# Revit family: Legrand Marina versión vertical referencias 036910 a 036950
name_source: partatom
category: Installations électriques
revit_build: Autodesk Revit 2018 (Build: 20170223_1515(x64)
units: mm (PartAtom-declared; Revit-internal decimal feet)

## family parameters
Basée sur le plan de construction = Non
Conserver l'orientation des annotations = Non
Cote de connecteur circulaire = Utiliser le diamètre
Couper avec des vides une fois chargée = Non
Numéro OmniClass = 23.80.00.00
Partagée = Non
Point de calcul de pièce = Non
Titre OmniClass = Electric Power and Lighting
Toujours verticalement = Oui
Type d'élément = Normal

## types (23) — shared parameters
Condiciones Generales de Uso = https://export.legrand.com
ETIM Class 6.0 = EC000058
Fabricant = Legrand
Formato cuadrado = Non
IK = 10
IP = 66
Materia = metálico
RAL = 7035
URL = www.legrand.fr
Versión horizontal = Non
Versión vertical = Oui
número de puertas = 1

## per-type parameters (varying)
- Legrand Atlantic 036913: Altura=500 mm  [stored 1.64042 ft]; Caja 036910=Non; Caja 036912=Non; Caja 036913=Oui; Caja 036917=Non; Caja 036918=Non; Caja 036919=Non; Caja 036920=Non; Caja 036921=Non; Caja 036925=Non; Caja 036926=Non; Caja 036930=Non; Caja 036931=Non; Caja 036932=Non; Caja 036933=Non; Caja 036937=Non; Caja 036938=Non; Caja 036939=Non; Caja 036942=Non; Caja 036943=Non; Caja 036944=Non; Caja 036945=Non; Caja 036946=Non; Caja 036950=Non; Longitud=400 mm  [stored 1.31234 ft]; peso=9.70 kg; profundidad=160 mm  [stored 0.524934 ft]
- Legrand Atlantic 036920: Altura=600 mm; Caja 036910=Non; Caja 036912=Non; Caja 036913=Non; Caja 036917=Non; Caja 036918=Non; Caja 036919=Non; Caja 036920=Oui; Caja 036921=Non; Caja 036925=Non; Caja 036926=Non; Caja 036930=Non; Caja 036931=Non; Caja 036932=Non; Caja 036933=Non; Caja 036937=Non; Caja 036938=Non; Caja 036939=Non; Caja 036942=Non; Caja 036943=Non; Caja 036944=Non; Caja 036945=Non; Caja 036946=Non; Caja 036950=Non; Longitud=500 mm  [stored 1.64042 ft]; peso=16.60 kg; profundidad=200 mm  [stored 0.656168 ft]
- Legrand Atlantic 036921: Altura=700 mm  [stored 2.29659 ft]; Caja 036910=Non; Caja 036912=Non; Caja 036913=Non; Caja 036917=Non; Caja 036918=Non; Caja 036919=Non; Caja 036920=Non; Caja 036921=Oui; Caja 036925=Non; Caja 036926=Non; Caja 036930=Non; Caja 036931=Non; Caja 036932=Non; Caja 036933=Non; Caja 036937=Non; Caja 036938=Non; Caja 036939=Non; Caja 036942=Non; Caja 036943=Non; Caja 036944=Non; Caja 036945=Non; Caja 036946=Non; Caja 036950=Non; Longitud=500 mm  [stored 1.64042 ft]; peso=18.40 kg; profundidad=200 mm  [stored 0.656168 ft]
- Legrand Atlantic 036942: Altura=1200 mm; Caja 036910=Non; Caja 036912=Non; Caja 036913=Non; Caja 036917=Non; Caja 036918=Non; Caja 036919=Non; Caja 036920=Non; Caja 036921=Non; Caja 036925=Non; Caja 036926=Non; Caja 036930=Non; Caja 036931=Non; Caja 036932=Non; Caja 036933=Non; Caja 036937=Non; Caja 036938=Non; Caja 036939=Non; Caja 036942=Oui; Caja 036943=Non; Caja 036944=Non; Caja 036945=Non; Caja 036946=Non; Caja 036950=Non; Longitud=600 mm; peso=47.00 kg; profundidad=300 mm
- Legrand Atlantic 036910: Altura=300 mm; Caja 036910=Oui; Caja 036912=Non; Caja 036913=Non; Caja 036917=Non; Caja 036918=Non; Caja 036919=Non; Caja 036920=Non; Caja 036921=Non; Caja 036925=Non; Caja 036926=Non; Caja 036930=Non; Caja 036931=Non; Caja 036932=Non; Caja 036933=Non; Caja 036937=Non; Caja 036938=Non; Caja 036939=Non; Caja 036942=Non; Caja 036943=Non; Caja 036944=Non; Caja 036945=Non; Caja 036946=Non; Caja 036950=Non; Longitud=200 mm  [stored 0.656168 ft]; peso=3.70 kg; profundidad=160 mm  [stored 0.524934 ft]
- Legrand Atlantic 036912: Altura=400 mm  [stored 1.31234 ft]; Caja 036910=Non; Caja 036912=Oui; Caja 036913=Non; Caja 036917=Non; Caja 036918=Non; Caja 036919=Non; Caja 036920=Non; Caja 036921=Non; Caja 036925=Non; Caja 036926=Non; Caja 036930=Non; Caja 036931=Non; Caja 036932=Non; Caja 036933=Non; Caja 036937=Non; Caja 036938=Non; Caja 036939=Non; Caja 036942=Non; Caja 036943=Non; Caja 036944=Non; Caja 036945=Non; Caja 036946=Non; Caja 036950=Non; Longitud=300 mm; peso=6.30 kg; profundidad=160 mm  [stored 0.524934 ft]
- Legrand Atlantic 036917: Altura=400 mm  [stored 1.31234 ft]; Caja 036910=Non; Caja 036912=Non; Caja 036913=Non; Caja 036917=Oui; Caja 036918=Non; Caja 036919=Non; Caja 036920=Non; Caja 036921=Non; Caja 036925=Non; Caja 036926=Non; Caja 036930=Non; Caja 036931=Non; Caja 036932=Non; Caja 036933=Non; Caja 036937=Non; Caja 036938=Non; Caja 036939=Non; Caja 036942=Non; Caja 036943=Non; Caja 036944=Non; Caja 036945=Non; Caja 036946=Non; Caja 036950=Non; Longitud=300 mm; peso=6.70 kg; profundidad=200 mm  [stored 0.656168 ft]
- Legrand Atlantic 036918: Altura=500 mm  [stored 1.64042 ft]; Caja 036910=Non; Caja 036912=Non; Caja 036913=Non; Caja 036917=Non; Caja 036918=Oui; Caja 036919=Non; Caja 036920=Non; Caja 036921=Non; Caja 036925=Non; Caja 036926=Non; Caja 036930=Non; Caja 036931=Non; Caja 036932=Non; Caja 036933=Non; Caja 036937=Non; Caja 036938=Non; Caja 036939=Non; Caja 036942=Non; Caja 036943=Non; Caja 036944=Non; Caja 036945=Non; Caja 036946=Non; Caja 036950=Non; Longitud=400 mm  [stored 1.31234 ft]; peso=10.60 kg; profundidad=160 mm  [stored 0.524934 ft]
- Legrand Atlantic 036919: Altura=600 mm; Caja 036910=Non; Caja 036912=Non; Caja 036913=Non; Caja 036917=Non; Caja 036918=Non; Caja 036919=Oui; Caja 036920=Non; Caja 036921=Non; Caja 036925=Non; Caja 036926=Non; Caja 036930=Non; Caja 036931=Non; Caja 036932=Non; Caja 036933=Non; Caja 036937=Non; Caja 036938=Non; Caja 036939=Non; Caja 036942=Non; Caja 036943=Non; Caja 036944=Non; Caja 036945=Non; Caja 036946=Non; Caja 036950=Non; Longitud=400 mm  [stored 1.31234 ft]; peso=12.00 kg; profundidad=160 mm  [stored 0.524934 ft]
- Legrand Atlantic 036925: Altura=500 mm  [stored 1.64042 ft]; Caja 036910=Non; Caja 036912=Non; Caja 036913=Non; Caja 036917=Non; Caja 036918=Non; Caja 036919=Non; Caja 036920=Non; Caja 036921=Non; Caja 036925=Oui; Caja 036926=Non; Caja 036930=Non; Caja 036931=Non; Caja 036932=Non; Caja 036933=Non; Caja 036937=Non; Caja 036938=Non; Caja 036939=Non; Caja 036942=Non; Caja 036943=Non; Caja 036944=Non; Caja 036945=Non; Caja 036946=Non; Caja 036950=Non; Longitud=400 mm  [stored 1.31234 ft]; peso=11.30 kg; profundidad=250 mm  [stored 0.82021 ft]
- Legrand Atlantic 036926: Altura=500 mm  [stored 1.64042 ft]; Caja 036910=Non; Caja 036912=Non; Caja 036913=Non; Caja 036917=Non; Caja 036918=Non; Caja 036919=Non; Caja 036920=Non; Caja 036921=Non; Caja 036925=Non; Caja 036926=Oui; Caja 036930=Non; Caja 036931=Non; Caja 036932=Non; Caja 036933=Non; Caja 036937=Non; Caja 036938=Non; Caja 036939=Non; Caja 036942=Non; Caja 036943=Non; Caja 036944=Non; Caja 036945=Non; Caja 036946=Non; Caja 036950=Non; Longitud=400 mm  [stored 1.31234 ft]; peso=12.80 kg; profundidad=250 mm  [stored 0.82021 ft]
- Legrand Atlantic 036930: Altura=700 mm  [stored 2.29659 ft]; Caja 036910=Non; Caja 036912=Non; Caja 036913=Non; Caja 036917=Non; Caja 036918=Non; Caja 036919=Non; Caja 036920=Non; Caja 036921=Non; Caja 036925=Non; Caja 036926=Non; Caja 036930=Oui; Caja 036931=Non; Caja 036932=Non; Caja 036933=Non; Caja 036937=Non; Caja 036938=Non; Caja 036939=Non; Caja 036942=Non; Caja 036943=Non; Caja 036944=Non; Caja 036945=Non; Caja 036946=Non; Caja 036950=Non; Longitud=500 mm  [stored 1.64042 ft]; peso=19.60 kg; profundidad=250 mm  [stored 0.82021 ft]
- Legrand Atlantic 036931: Altura=800 mm  [stored 2.62467 ft]; Caja 036910=Non; Caja 036912=Non; Caja 036913=Non; Caja 036917=Non; Caja 036918=Non; Caja 036919=Non; Caja 036920=Non; Caja 036921=Non; Caja 036925=Non; Caja 036926=Non; Caja 036930=Non; Caja 036931=Oui; Caja 036932=Non; Caja 036933=Non; Caja 036937=Non; Caja 036938=Non; Caja 036939=Non; Caja 036942=Non; Caja 036943=Non; Caja 036944=Non; Caja 036945=Non; Caja 036946=Non; Caja 036950=Non; Longitud=600 mm; peso=26.60 kg; profundidad=250 mm  [stored 0.82021 ft]
- Legrand Atlantic 036932: Altura=1000 mm  [stored 3.28084 ft]; Caja 036910=Non; Caja 036912=Non; Caja 036913=Non; Caja 036917=Non; Caja 036918=Non; Caja 036919=Non; Caja 036920=Non; Caja 036921=Non; Caja 036925=Non; Caja 036926=Non; Caja 036930=Non; Caja 036931=Non; Caja 036932=Oui; Caja 036933=Non; Caja 036937=Non; Caja 036938=Non; Caja 036939=Non; Caja 036942=Non; Caja 036943=Non; Caja 036944=Non; Caja 036945=Non; Caja 036946=Non; Caja 036950=Non; Longitud=600 mm; peso=36.20 kg; profundidad=250 mm  [stored 0.82021 ft]
- Legrand Atlantic 036933: Altura=1000 mm  [stored 3.28084 ft]; Caja 036910=Non; Caja 036912=Non; Caja 036913=Non; Caja 036917=Non; Caja 036918=Non; Caja 036919=Non; Caja 036920=Non; Caja 036921=Non; Caja 036925=Non; Caja 036926=Non; Caja 036930=Non; Caja 036931=Non; Caja 036932=Non; Caja 036933=Oui; Caja 036937=Non; Caja 036938=Non; Caja 036939=Non; Caja 036942=Non; Caja 036943=Non; Caja 036944=Non; Caja 036945=Non; Caja 036946=Non; Caja 036950=Non; Longitud=800 mm  [stored 2.62467 ft]; peso=46.80 kg; profundidad=250 mm  [stored 0.82021 ft]
- Legrand Atlantic 036937: Altura=800 mm  [stored 2.62467 ft]; Caja 036910=Non; Caja 036912=Non; Caja 036913=Non; Caja 036917=Non; Caja 036918=Non; Caja 036919=Non; Caja 036920=Non; Caja 036921=Non; Caja 036925=Non; Caja 036926=Non; Caja 036930=Non; Caja 036931=Non; Caja 036932=Non; Caja 036933=Non; Caja 036937=Oui; Caja 036938=Non; Caja 036939=Non; Caja 036942=Non; Caja 036943=Non; Caja 036944=Non; Caja 036945=Non; Caja 036946=Non; Caja 036950=Non; Longitud=600 mm; peso=28.80 kg; profundidad=300 mm
- Legrand Atlantic 036938: Altura=1000 mm  [stored 3.28084 ft]; Caja 036910=Non; Caja 036912=Non; Caja 036913=Non; Caja 036917=Non; Caja 036918=Non; Caja 036919=Non; Caja 036920=Non; Caja 036921=Non; Caja 036925=Non; Caja 036926=Non; Caja 036930=Non; Caja 036931=Non; Caja 036932=Non; Caja 036933=Non; Caja 036937=Non; Caja 036938=Oui; Caja 036939=Non; Caja 036942=Non; Caja 036943=Non; Caja 036944=Non; Caja 036945=Non; Caja 036946=Non; Caja 036950=Non; Longitud=600 mm; peso=37.80 kg; profundidad=300 mm
- Legrand Atlantic 036939: Altura=1000 mm  [stored 3.28084 ft]; Caja 036910=Non; Caja 036912=Non; Caja 036913=Non; Caja 036917=Non; Caja 036918=Non; Caja 036919=Non; Caja 036920=Non; Caja 036921=Non; Caja 036925=Non; Caja 036926=Non; Caja 036930=Non; Caja 036931=Non; Caja 036932=Non; Caja 036933=Non; Caja 036937=Non; Caja 036938=Non; Caja 036939=Oui; Caja 036942=Non; Caja 036943=Non; Caja 036944=Non; Caja 036945=Non; Caja 036946=Non; Caja 036950=Non; Longitud=800 mm  [stored 2.62467 ft]; peso=50.50 kg; profundidad=300 mm
- Legrand Atlantic 036943: Altura=1200 mm; Caja 036910=Non; Caja 036912=Non; Caja 036913=Non; Caja 036917=Non; Caja 036918=Non; Caja 036919=Non; Caja 036920=Non; Caja 036921=Non; Caja 036925=Non; Caja 036926=Non; Caja 036930=Non; Caja 036931=Non; Caja 036932=Non; Caja 036933=Non; Caja 036937=Non; Caja 036938=Non; Caja 036939=Non; Caja 036942=Non; Caja 036943=Oui; Caja 036944=Non; Caja 036945=Non; Caja 036946=Non; Caja 036950=Non; Longitud=800 mm  [stored 2.62467 ft]; peso=62.20 kg; profundidad=300 mm
- Legrand Atlantic 036944: Altura=800 mm  [stored 2.62467 ft]; Caja 036910=Non; Caja 036912=Non; Caja 036913=Non; Caja 036917=Non; Caja 036918=Non; Caja 036919=Non; Caja 036920=Non; Caja 036921=Non; Caja 036925=Non; Caja 036926=Non; Caja 036930=Non; Caja 036931=Non; Caja 036932=Non; Caja 036933=Non; Caja 036937=Non; Caja 036938=Non; Caja 036939=Non; Caja 036942=Non; Caja 036943=Non; Caja 036944=Oui; Caja 036945=Non; Caja 036946=Non; Caja 036950=Non; Longitud=600 mm; peso=36.80 kg; profundidad=400 mm  [stored 1.31234 ft]
- Legrand Atlantic 036945: Altura=1000 mm  [stored 3.28084 ft]; Caja 036910=Non; Caja 036912=Non; Caja 036913=Non; Caja 036917=Non; Caja 036918=Non; Caja 036919=Non; Caja 036920=Non; Caja 036921=Non; Caja 036925=Non; Caja 036926=Non; Caja 036930=Non; Caja 036931=Non; Caja 036932=Non; Caja 036933=Non; Caja 036937=Non; Caja 036938=Non; Caja 036939=Non; Caja 036942=Non; Caja 036943=Non; Caja 036944=Non; Caja 036945=Oui; Caja 036946=Non; Caja 036950=Non; Longitud=800 mm  [stored 2.62467 ft]; peso=62.30 kg; profundidad=400 mm  [stored 1.31234 ft]
- Legrand Atlantic 036946: Altura=1200 mm; Caja 036910=Non; Caja 036912=Non; Caja 036913=Non; Caja 036917=Non; Caja 036918=Non; Caja 036919=Non; Caja 036920=Non; Caja 036921=Non; Caja 036925=Non; Caja 036926=Non; Caja 036930=Non; Caja 036931=Non; Caja 036932=Non; Caja 036933=Non; Caja 036937=Non; Caja 036938=Non; Caja 036939=Non; Caja 036942=Non; Caja 036943=Non; Caja 036944=Non; Caja 036945=Non; Caja 036946=Oui; Caja 036950=Non; Longitud=800 mm  [stored 2.62467 ft]; peso=76.00 kg; profundidad=400 mm  [stored 1.31234 ft]
- Legrand Atlantic 036950: Altura=1400 mm  [stored 4.59318 ft]; Caja 036910=Non; Caja 036912=Non; Caja 036913=Non; Caja 036917=Non; Caja 036918=Non; Caja 036919=Non; Caja 036920=Non; Caja 036921=Non; Caja 036925=Non; Caja 036926=Non; Caja 036930=Non; Caja 036931=Non; Caja 036932=Non; Caja 036933=Non; Caja 036937=Non; Caja 036938=Non; Caja 036939=Non; Caja 036942=Non; Caja 036943=Non; Caja 036944=Non; Caja 036945=Non; Caja 036946=Non; Caja 036950=Oui; Longitud=800 mm  [stored 2.62467 ft]; peso=80.90 kg; profundidad=400 mm  [stored 1.31234 ft]

note: column(s) folded — value = type name in every type: Description

note: [stored X ft] marks values corroborated as IEEE doubles in the binary element streams (Revit-internal decimal feet)
